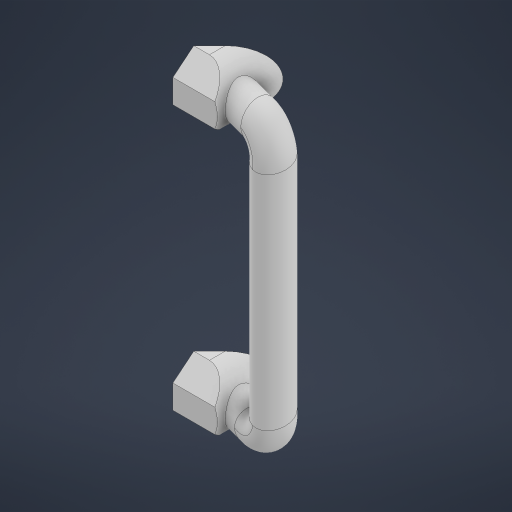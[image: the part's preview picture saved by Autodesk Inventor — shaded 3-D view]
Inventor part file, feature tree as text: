
AUTODESK INVENTOR PART (.ipt)
format: ipt  version: 2024 (Build 280153000, 153)  size: 315,904 bytes
history: native  units: in
note: dims shown in document units (in); Inventor stores cm internally (conversion verified against a paired STEP export)
features: reference x9, sketch x7, plane x7, extrude x4, other x3, projected_geometry x2, sweep x1
ambient origin geometry x8: Origin, YZ Plane, XZ Plane, XY Plane, X Axis, Y Axis, Z Axis, Center Point
bodies: Solid1 (feature_tree)
feature tree (33):
  sketch  "Sketch1"  dims[d0=1.0in d1=0.0in d2=0.1654in]
  plane  "Work Plane1"
  extrude  "Extrusion1"  Depth=0.1654in
  plane  "Work Plane2"
  extrude  "Extrusion2"  Depth=1.0in TaperAngle=0.0deg
  plane  "Work Plane3"
  extrude  "Extrusion3"  Depth=0.1181in TaperAngle=0.0deg
  extrude  "Extrusion4"  Depth=0.25in
  plane  "Work Plane5"
  sketch  "Sketch5"  dims[d13=-0.3937in d14=0.3937in]
  plane  "Work Plane6"
  sketch  "Sketch6"  dims[d17=120.0deg d18=-0.1772in]
  plane  "Work Plane8"
  sweep  "Sweep2"
  reference  "Reference1"
  reference  "Reference2"
  reference  "Reference3"
  reference  "Reference4"
  reference  "Reference5"
  reference  "Reference6"
  sketch  "Sketch2"  dims[d3=0.1654in d4=1.0in d5=0.0in]
  reference  "Reference7"
  reference  "Reference8"
  sketch  "Sketch3"  dims[d6=1.0in d7=0.0in d8=0.1181in d9=0.0in]
  reference  "Reference9"
  sketch  "Sketch4"  dims[d11=-0.0787in d12=0.25in]
  projected_geometry  "Projected Loop1"
  projected_geometry  "Projected Loop2"
  plane  "Work Plane7"
  sketch  "Sketch8"  dims[d19=0.0in d20=0.0in]
  other  "<userpath>\Desktop\SeniorDesign\Head_V3\Head_V3_Assembly.iam"
  other  "Head_V3_Assembly.iam"
  other  "Head_Top:1"
